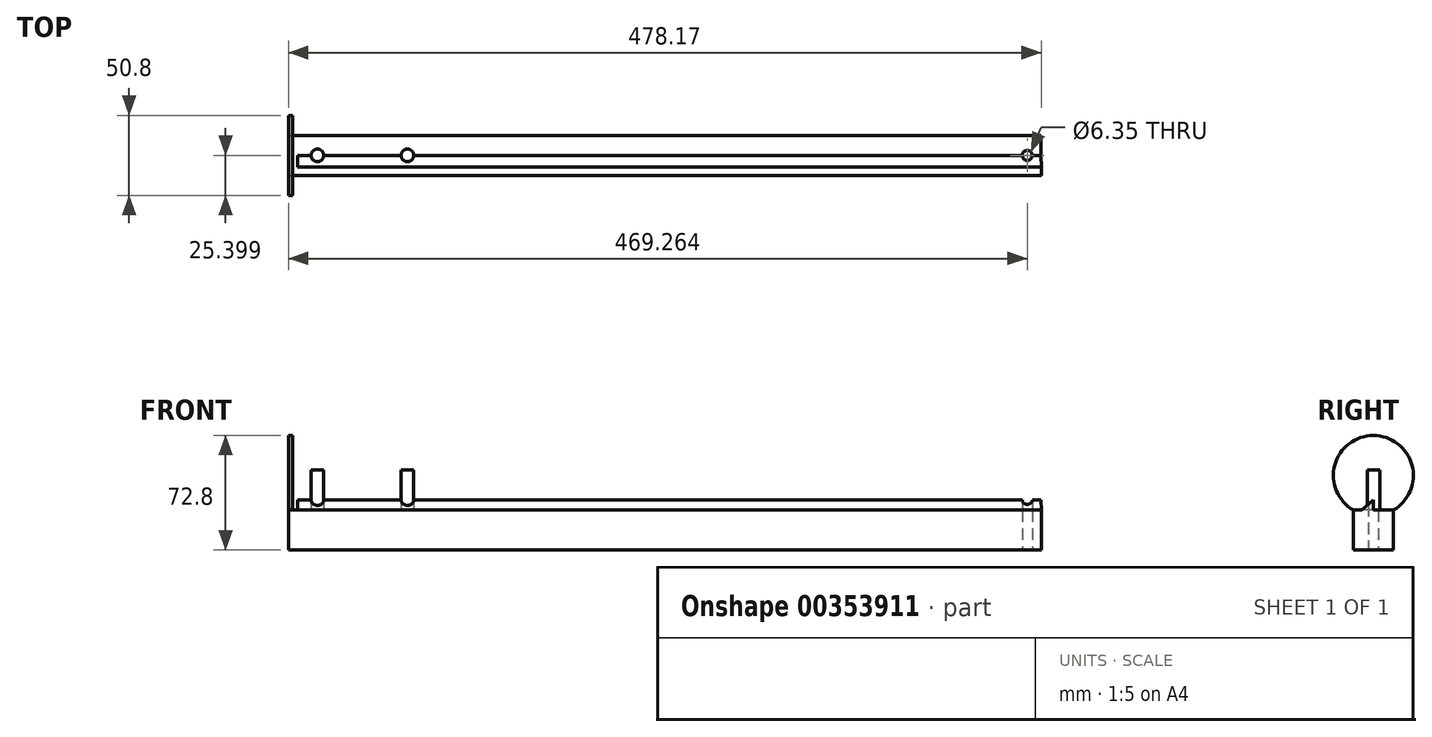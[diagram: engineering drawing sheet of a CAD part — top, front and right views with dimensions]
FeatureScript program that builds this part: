
annotation { "Feature Type Name" : "Feature", "Feature Type Description" : "" }
export const myFeature = defineFeature(function(context is Context, id is Id, definition is map)
    precondition{}
    {
        {
            var Q0;
            Q0=qCreatedBy(makeId("Top.planeOp"),FACE);
            var sketch = newSketch(context, id + "F0", { "sketchPlane" : qUnion([Q0])});
            skLineSegment(sketch, "E0.bottom", {"start": v(-29.88, 14.87) * mm, "end": v(478.12, 14.87) * mm});
            skLineSegment(sketch, "E0.top", {"start": v(-29.88, -10.53) * mm, "end": v(478.12, -10.53) * mm});
            skLineSegment(sketch, "E0.left", {"start": v(-29.88, 14.87) * mm, "end": v(-29.88, -10.53) * mm});
            skLineSegment(sketch, "E0.right", {"start": v(478.12, 14.87) * mm, "end": v(478.12, -10.53) * mm});
            skSolve(sketch);
        }
        {
            var Q0;
            Q0 = qSketchRegion(id + "F0", true);
            extrude(context, id + "F1", {"entities" : qUnion([Q0]), "depth" : 25.4 * mm});
        }
        {
            var Q0;
            Q0=makeQuery(id+"F1.opExtrude","SWEPT_FACE",FACE,{"disambiguationData":[OSD([sQuery(id+"F0.wireOp",EDGE,"E0.left")])]});
            var sketch = newSketch(context, id + "F2", { "sketchPlane" : qUnion([Q0])});
            skPoint(sketch, "E1.endSnap0", {"position": v(-2.17, 25.4) * mm});
            skLineSegment(sketch, "E2", {"start": v(-2.17, 31.75) * mm, "end": v(-9.59, 25.4) * mm});
            skLineSegment(sketch, "E3", {"start": v(-9.59, 25.4) * mm, "end": v(-2.17, 31.75) * mm});
            skLineSegment(sketch, "E4", {"start": v(-2.17, 31.75) * mm, "end": v(-2.17, 25.4) * mm});
            skLineSegment(sketch, "E5.MirrorCS", {"start": v(5.25, 25.4) * mm, "end": v(-2.17, 31.75) * mm});
            skSolve(sketch);
        }
        {
            var Q0;
            Q0 = qSketchRegion(id + "F2", true);
            var Q1;
            {var subQ0=sQuery(id+"F2.wireOp",EDGE,"E3");Q1=makeQuery(id+"F2.imprint","IMPRINT",FACE,{"disambiguationData":[TD([[makeQuery(id+"F2.imprint","IMPRINT",EDGE,{"derivedFrom":subQ0}),-1.0]])]});}
            var Q2;
            {var subQ0=sQuery(id+"F2.wireOp",EDGE,"E4");Q2=makeQuery(id+"F2.imprint","IMPRINT",FACE,{"disambiguationData":[TD([[makeQuery(id+"F2.imprint","IMPRINT",EDGE,{"derivedFrom":subQ0}),1.0]])]});}
            extrude(context, id + "F3", {"entities" : qUnion([Q0, Q1, Q2]), "operationType" : NewBodyOperationType.ADD, "endBound" : BoundingType.THROUGH_ALL, "oppositeDirection" : true, "depth" : 25.4 * mm});
        }
        {
            var Q0;
            Q0=qCreatedBy(makeId("Top.planeOp"),FACE);
            var sketch = newSketch(context, id + "F4", { "sketchPlane" : qUnion([Q0])});
            skCircle(sketch, "E6", {"center": v(-17.18, 2.2) * mm, "radius": 3.97 * mm});
            skCircle(sketch, "E7", {"center": v(39.97, 2.2) * mm, "radius": 3.98 * mm});
            skSolve(sketch);
        }
        {
            var Q0;
            Q0 = qSketchRegion(id + "F4", true);
            extrude(context, id + "F5", {"entities" : qUnion([Q0]), "operationType" : NewBodyOperationType.ADD, "depth" : 50.8 * mm});
        }
        {
            var Q0;
            Q0=qCreatedBy(makeId("Top.planeOp"),FACE);
            var sketch = newSketch(context, id + "F6", { "sketchPlane" : qUnion([Q0])});
            skCircle(sketch, "E8", {"center": v(433.67, 2.17) * mm, "radius": 3.18 * mm});
            skSolve(sketch);
        }
        {
            var Q0;
            Q0 = qSketchRegion(id + "F6", true);
            extrude(context, id + "F7", {"entities" : qUnion([Q0]), "operationType" : NewBodyOperationType.REMOVE, "depth" : 84.33 * mm, "hasSecondDirection" : true, "secondDirectionOppositeDirection" : true, "secondDirectionDepth" : 61.47 * mm});
        }
        {
            var Q0;
            Q0=qCreatedBy(makeId("Top.planeOp"),FACE);
            var sketch = newSketch(context, id + "F8", { "sketchPlane" : qUnion([Q0])});
            skLineSegment(sketch, "E9", {"start": v(442.06, 27.37) * mm, "end": v(442.76, -23.43) * mm});
            skLineSegment(sketch, "E10", {"start": v(442.76, -23.43) * mm, "end": v(487.52, -22.82) * mm});
            skLineSegment(sketch, "E11", {"start": v(487.52, -22.82) * mm, "end": v(487.52, 27.37) * mm});
            skLineSegment(sketch, "E12", {"start": v(487.52, 27.37) * mm, "end": v(442.06, 27.37) * mm});
            skSolve(sketch);
        }
        {
            var Q0;
            Q0 = qSketchRegion(id + "F8", true);
            extrude(context, id + "F9", {"entities" : qUnion([Q0]), "depth" : 25.4 * mm});
        }
        {
            var Q0;
            Q0 = qSketchRegion(id + "F8", true);
            extrude(context, id + "F10", {"entities" : qUnion([Q0]), "operationType" : NewBodyOperationType.REMOVE, "depth" : 148.6 * mm});
        }
        {
            var Q0;
            {var subQ0=sQuery(id+"F0.wireOp",EDGE,"E0.left");Q0=makeQuery(id+"F3.boolean.opBoolean","MERGE",FACE,{"derivedFrom":[makeQuery(id+"F1.opExtrude","SWEPT_FACE",FACE,{"disambiguationData":[OSD([subQ0])]}),makeQuery(id+"F3.opExtrude","CAP_FACE",FACE,{"disambiguationData":[OSD([subQ0,sQuery(id+"F2.wireOp",EDGE,"E3"),sQuery(id+"F2.wireOp",EDGE,"E5.MirrorCS")])],"isStart":true})]});}
            var sketch = newSketch(context, id + "F11", { "sketchPlane" : qUnion([Q0])});
            skLineSegment(sketch, "E13.bottom", {"start": v(-14.87, 25.4) * mm, "end": v(10.53, 25.4) * mm});
            skLineSegment(sketch, "E13.top", {"start": v(-14.87, 0) * mm, "end": v(10.53, 0) * mm});
            skLineSegment(sketch, "E13.left", {"start": v(-14.87, 25.4) * mm, "end": v(-14.87, 0) * mm});
            skLineSegment(sketch, "E13.right", {"start": v(10.53, 25.4) * mm, "end": v(10.53, 0) * mm});
            skSolve(sketch);
        }
        {
            var Q0;
            Q0 = qSketchRegion(id + "F11", true);
            extrude(context, id + "F12", {"entities" : qUnion([Q0]), "operationType" : NewBodyOperationType.ADD, "depth" : 3.17 * mm});
        }
        {
            var Q0;
            Q0=makeQuery(id+"F12.opExtrude","CAP_FACE",FACE,{"disambiguationData":[OSD([sQuery(id+"F11.wireOp",EDGE,"E13.bottom"),sQuery(id+"F11.wireOp",EDGE,"E13.top"),sQuery(id+"F11.wireOp",EDGE,"E13.left"),sQuery(id+"F11.wireOp",EDGE,"E13.right")])],"isStart":false});
            var sketch = newSketch(context, id + "F13", { "sketchPlane" : qUnion([Q0])});
            skLineSegment(sketch, "E14.bottom", {"start": v(-14.87, 25.4) * mm, "end": v(10.53, 25.4) * mm});
            skLineSegment(sketch, "E14.top", {"start": v(-14.87, 0) * mm, "end": v(10.53, 0) * mm});
            skLineSegment(sketch, "E14.left", {"start": v(-14.87, 25.4) * mm, "end": v(-14.87, 0) * mm});
            skLineSegment(sketch, "E14.right", {"start": v(10.53, 25.4) * mm, "end": v(10.53, 0) * mm});
            skArc(sketch, "E15", {"start": v(10.53, 25.4) * mm, "mid": v(-2.17, 72.8) * mm, "end": v(-14.87, 25.4) * mm});
            skSolve(sketch);
        }
        {
            var Q0;
            Q0 = qSketchRegion(id + "F13", true);
            extrude(context, id + "F14", {"entities" : qUnion([Q0]), "operationType" : NewBodyOperationType.ADD, "depth" : 2.54 * mm});
        }
    });
